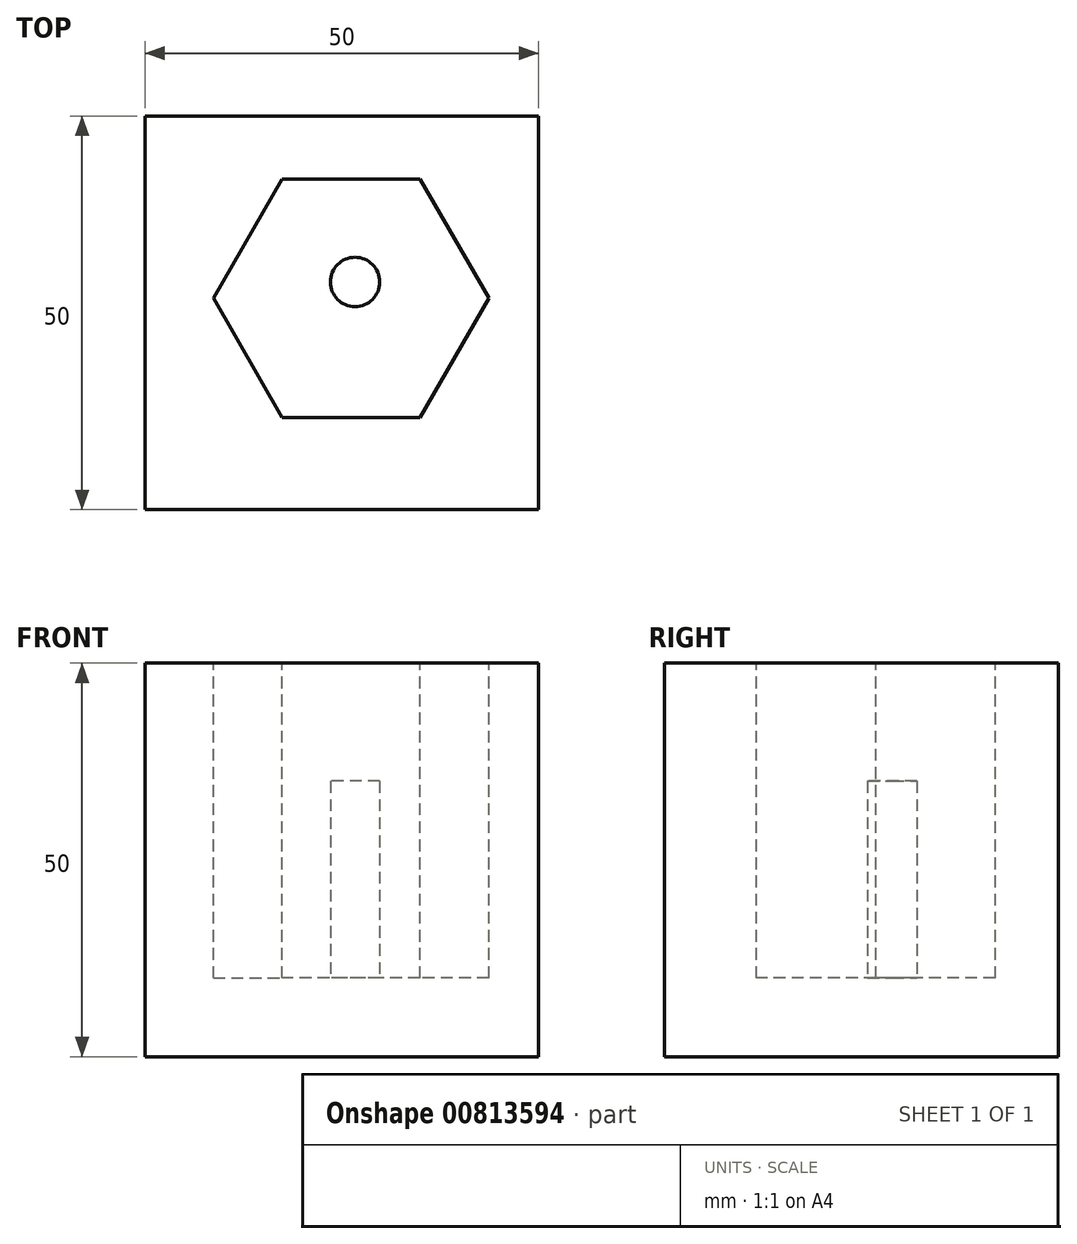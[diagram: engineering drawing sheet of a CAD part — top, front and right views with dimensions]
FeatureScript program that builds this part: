
annotation { "Feature Type Name" : "Feature", "Feature Type Description" : "" }
export const myFeature = defineFeature(function(context is Context, id is Id, definition is map)
    precondition{}
    {
        {
            var Q0;
            Q0=qCreatedBy(makeId("Top.planeOp"),FACE);
            var sketch = newSketch(context, id + "F0", { "sketchPlane" : qUnion([Q0])});
            skLineSegment(sketch, "E0.bottom", {"start": v(-23.4, 23.15) * mm, "end": v(26.6, 23.15) * mm});
            skLineSegment(sketch, "E0.top", {"start": v(-23.4, -26.85) * mm, "end": v(26.6, -26.85) * mm});
            skLineSegment(sketch, "E0.left", {"start": v(-23.4, 23.15) * mm, "end": v(-23.4, -26.85) * mm});
            skLineSegment(sketch, "E0.right", {"start": v(26.6, 23.15) * mm, "end": v(26.6, -26.85) * mm});
            skSolve(sketch);
        }
        {
            var Q0;
            Q0 = qSketchRegion(id + "F0", true);
            extrude(context, id + "F1", {"entities" : qUnion([Q0]), "depth" : 50 * mm, "offsetDistance" : 25 * mm});
        }
        {
            var Q0;
            Q0=makeQuery(id+"F1.opExtrude","CAP_FACE",FACE,{"disambiguationData":[OSD([sQuery(id+"F0.wireOp",EDGE,"E0.bottom"),sQuery(id+"F0.wireOp",EDGE,"E0.top"),sQuery(id+"F0.wireOp",EDGE,"E0.left"),sQuery(id+"F0.wireOp",EDGE,"E0.right")])],"isStart":false});
            var sketch = newSketch(context, id + "F2", { "sketchPlane" : qUnion([Q0])});
            skCircle(sketch, "E1.cCircle", {"center": v(2.78, 0) * mm, "radius": 15.16 * mm, "construction": true});
            skLineSegment(sketch, "E1.0", {"start": v(11.53, -15.16) * mm, "end": v(-5.97, -15.16) * mm});
            skLineSegment(sketch, "E1.1", {"start": v(-5.97, -15.16) * mm, "end": v(-14.72, 0) * mm});
            skLineSegment(sketch, "E1.2", {"start": v(-14.72, 0) * mm, "end": v(-5.97, 15.16) * mm});
            skLineSegment(sketch, "E1.3", {"start": v(-5.97, 15.16) * mm, "end": v(11.53, 15.16) * mm});
            skLineSegment(sketch, "E1.4", {"start": v(11.53, 15.16) * mm, "end": v(20.28, 0) * mm});
            skLineSegment(sketch, "E1.5", {"start": v(20.28, 0) * mm, "end": v(11.53, -15.16) * mm});
            skPoint(sketch, "E1.0.midPoint", {"position": v(2.78, -15.16) * mm});
            skSolve(sketch);
        }
        {
            var Q0;
            Q0 = qSketchRegion(id + "F2", true);
            extrude(context, id + "F3", {"entities" : qUnion([Q0]), "operationType" : NewBodyOperationType.REMOVE, "oppositeDirection" : true, "depth" : 40 * mm, "offsetDistance" : 25 * mm});
        }
        {
            var Q0;
            Q0=makeQuery(id+"F3.boolean.opBoolean","COPY",FACE,{"derivedFrom":makeQuery(id+"F3.opExtrude","CAP_FACE",FACE,{"disambiguationData":[OSD([sQuery(id+"F2.wireOp",EDGE,"E1.0"),sQuery(id+"F2.wireOp",EDGE,"E1.1"),sQuery(id+"F2.wireOp",EDGE,"E1.2"),sQuery(id+"F2.wireOp",EDGE,"E1.3"),sQuery(id+"F2.wireOp",EDGE,"E1.4"),sQuery(id+"F2.wireOp",EDGE,"E1.5")])],"isStart":false})});
            var sketch = newSketch(context, id + "F4", { "sketchPlane" : qUnion([Q0])});
            skCircle(sketch, "E2", {"center": v(3.28, 2.06) * mm, "radius": 3.14 * mm});
            skSolve(sketch);
        }
        {
            var Q0;
            Q0 = qSketchRegion(id + "F4", true);
            extrude(context, id + "F5", {"entities" : qUnion([Q0]), "operationType" : NewBodyOperationType.ADD, "depth" : 25 * mm, "offsetDistance" : 25 * mm});
        }
    });
